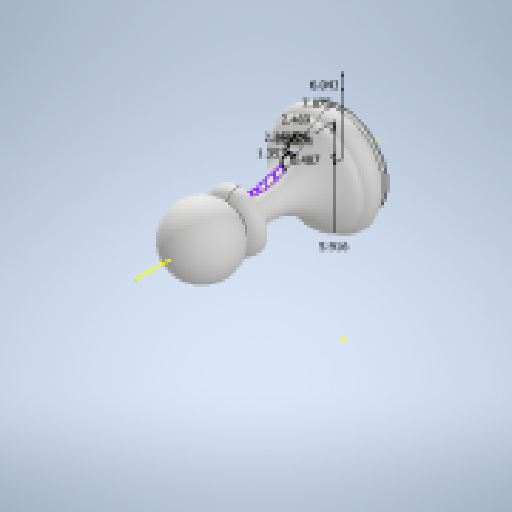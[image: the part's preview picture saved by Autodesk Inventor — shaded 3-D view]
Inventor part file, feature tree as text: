
AUTODESK INVENTOR PART (.ipt)
format: ipt  version: 2024.1 (Build 281209000, 209)  size: 1,632,256 bytes
history: native  units: mm
features: other x13, sketch x10, extrude x7, pattern_circular x3, revolve x1, chamfer x1, plane x1, emboss x1, helix x1, projected_geometry x1
ambient origin geometry x8: Origin, YZ Plane, XZ Plane, XY Plane, X Axis, Y Axis, Z Axis, Center Point
bodies: Solid1 (feature_tree)
feature tree (39):
  extrude  "Extrusion1"  Depth=3.0mm TaperAngle=0.0deg
  other  "Work Axis1"
  extrude  "Extrusion2"  Depth=23.0mm
  revolve  "Revolution1"  [1 undecoded]
  chamfer  "Chamfer1"  Distance=3.0mm
  sketch  "Sketch11"  dims[d37=120.0mm d38=360.0deg d40=10.0mm d41=0.0mm]
  extrude  "Extrusion6"  Depth=2.0mm TaperAngle=0.0deg
  extrude  "Extrusion7"  Depth=0.3mm TaperAngle=0.0deg
  extrude  "Extrusion8"  Depth=10.0mm TaperAngle=0.0deg
  extrude  "Extrusion9"  Depth=0.4mm TaperAngle=0.0deg
  pattern_circular  "Circular Pattern4"  [2 undecoded]
  plane  "Work Plane5"
  sketch  "3D Sketch3"
  emboss  "Emboss1"
  pattern_circular  "Circular Pattern3"  [2 undecoded]
  helix  "Coil1"  [1 undecoded]
  extrude  "Extrusion4"  Depth=5.915933mm
  pattern_circular  "Circular Pattern2"  [2 undecoded]
  sketch  "Sketch1"  dims[d0=10.0mm d1=3.0mm d2=0.0mm]
  sketch  "Sketch2"  dims[d3=10.5mm d4=23.0mm]
  sketch  "Sketch3"  dims[d5=360.0deg d6=14.3mm d7=3.0mm d8=0.0mm]
  projected_geometry  "Projected Loop1"
  sketch  "Sketch5"  dims[d9=0.5mm d10=2.0mm d11=45.0deg d17=2.0mm d18=0.0mm]
  sketch  "Sketch6"  dims[d19=100.0mm d20=360.0deg]
  sketch  "Sketch9"  dims[d22=1.0mm d23=10.0mm d24=50.0mm d25=-0.174533mm d26=90.0deg d27=90.0deg d28=0.0mm d29=0.0mm d35=0.3mm d36=0.0mm]
  other  "Work Axis2"
  other  "Work Axis3"
  other  "Work Axis4"
  other  "Work Axis5"
  other  "Work Axis6"
  other  "Work Axis7"
  other  "Work Axis8"
  other  "Work Axis9"
  other  "Work Axis10"
  other  "Work Axis11"
  other  "Work Axis12"
  other  "Curve On Face1"
  sketch  "Sketch12"  dims[d42=4.15mm d43=0.0mm d44=0.4mm d45=0.0mm]
  sketch  "Sketch13"  dims[d51=6.042539mm d52=2.314913mm d53=2.489147mm d54=7.875064mm d55=5.915933mm d57=0.487336mm d58=0.259822mm d59=1.352868mm d60=2.004443mm d61=0.435462mm d64=10.0mm d65=0.0mm d66=5.0mm d67=0.3mm d68=0.0mm d69=0.0mm d70=60.0mm d71=360.0deg]
note: 8 required parameter values undecoded (feature->parameter linkage not recoverable at this tier; creation-order binding heuristic only, values carry confidence <= 0.55)